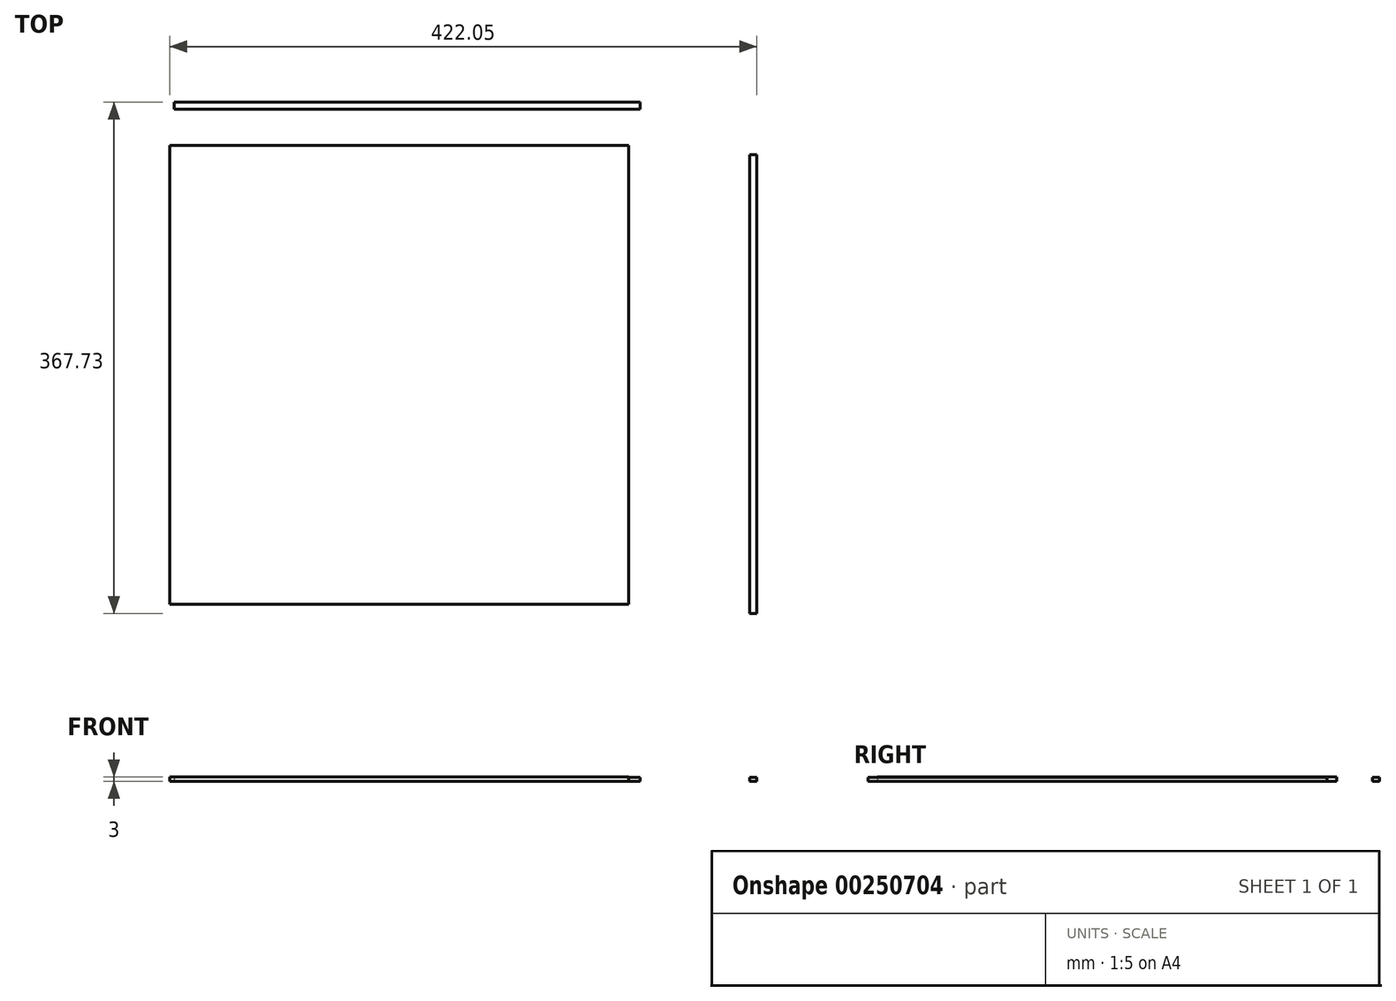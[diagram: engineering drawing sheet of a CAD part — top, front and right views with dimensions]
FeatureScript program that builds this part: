
annotation { "Feature Type Name" : "Feature", "Feature Type Description" : "" }
export const myFeature = defineFeature(function(context is Context, id is Id, definition is map)
    precondition{}
    {
        {
            var Q0;
            Q0=qCreatedBy(makeId("Top.planeOp"),FACE);
            var sketch = newSketch(context, id + "F0", { "sketchPlane" : qUnion([Q0])});
            skLineSegment(sketch, "E0.bottom", {"start": v(-165, 165) * mm, "end": v(165, 165) * mm});
            skLineSegment(sketch, "E0.top", {"start": v(-165, -165) * mm, "end": v(165, -165) * mm});
            skLineSegment(sketch, "E0.left", {"start": v(-165, 165) * mm, "end": v(-165, -165) * mm});
            skLineSegment(sketch, "E0.right", {"start": v(165, 165) * mm, "end": v(165, -165) * mm});
            skSolve(sketch);
        }
        {
            var Q0;
            Q0=makeQuery(id+"F0.imprint","IMPRINT",FACE,{"disambiguationData":[TD([[makeQuery(id+"F0.imprint","IMPRINT",EDGE,{"derivedFrom":sQuery(id+"F0.wireOp",EDGE,"E0.bottom")}),-1.0]])]});
            extrude(context, id + "F1", {"entities" : qUnion([Q0]), "depth" : 3 * mm});
        }
        {
            var Q0;
            Q0=qCreatedBy(makeId("Top.planeOp"),FACE);
            var sketch = newSketch(context, id + "F2", { "sketchPlane" : qUnion([Q0])});
            skLineSegment(sketch, "E1.bottom", {"start": v(252.05, 158.22) * mm, "end": v(257.05, 158.22) * mm});
            skLineSegment(sketch, "E1.top", {"start": v(252.05, -171.78) * mm, "end": v(257.05, -171.78) * mm});
            skLineSegment(sketch, "E1.left", {"start": v(252.05, 158.22) * mm, "end": v(252.05, -171.78) * mm});
            skLineSegment(sketch, "E1.right", {"start": v(257.05, 158.22) * mm, "end": v(257.05, -171.78) * mm});
            skSolve(sketch);
        }
        {
            var Q0;
            Q0=makeQuery(id+"F2.imprint","IMPRINT",FACE,{"disambiguationData":[TD([[makeQuery(id+"F2.imprint","IMPRINT",EDGE,{"derivedFrom":sQuery(id+"F2.wireOp",EDGE,"E1.bottom")}),-1.0]])]});
            extrude(context, id + "F3", {"entities" : qUnion([Q0]), "depth" : 2.8 * mm});
        }
        {
            var Q0;
            Q0=qCreatedBy(makeId("Top.planeOp"),FACE);
            var sketch = newSketch(context, id + "F4", { "sketchPlane" : qUnion([Q0])});
            skLineSegment(sketch, "E2.bottom", {"start": v(-161.78, 195.95) * mm, "end": v(173.22, 195.95) * mm});
            skLineSegment(sketch, "E2.top", {"start": v(-161.78, 190.95) * mm, "end": v(173.22, 190.95) * mm});
            skLineSegment(sketch, "E2.left", {"start": v(-161.78, 195.95) * mm, "end": v(-161.78, 190.95) * mm});
            skLineSegment(sketch, "E2.right", {"start": v(173.22, 195.95) * mm, "end": v(173.22, 190.95) * mm});
            skSolve(sketch);
        }
        {
            var Q0;
            Q0=makeQuery(id+"F4.imprint","IMPRINT",FACE,{"disambiguationData":[TD([[makeQuery(id+"F4.imprint","IMPRINT",EDGE,{"derivedFrom":sQuery(id+"F4.wireOp",EDGE,"E2.bottom")}),-1.0]])]});
            extrude(context, id + "F5", {"entities" : qUnion([Q0]), "depth" : 2.8 * mm});
        }
    });
